FREECAD ASSEMBLY — COMPONENT RECIPES ("BoxAssembly")

This assembly document has 2 components, labeled P0..P1 below (a component is one placed body or linked part). 0 of them carry a construction recipe — the FreeCAD feature program that regenerates the part from scratch, quoted from this document or its linked companion documents; the rest are supplied as boundary geometry only. No exploded tour is included for this assembly.
COMPONENT P0 — geometry summary ("Cuerpo"; no construction recipe available for this part):
  bounding box: 105.0 x 105.0 x 105.0 mm
  tessellated surface: 12,656 triangles
  volume: 275667 mm^3 (24% of its bounding box)
  symmetry: mirror-symmetric across its y mid-plane
COMPONENT P1 — geometry summary ("Cuerpo001"; no construction recipe available for this part):
  bounding box: 105.0 x 105.0 x 15.0 mm
  tessellated surface: 28,132 triangles
  volume: 59507 mm^3 (36% of its bounding box)
PROVENANCE & LICENSES
A FreeCAD (.FCStd) document from a public repository crawl; recipes are the document's own serialized feature recipes (and, for linked parts, companion documents' recipes).
License: as declared in the source repository (recorded in the dataset sidecar).
